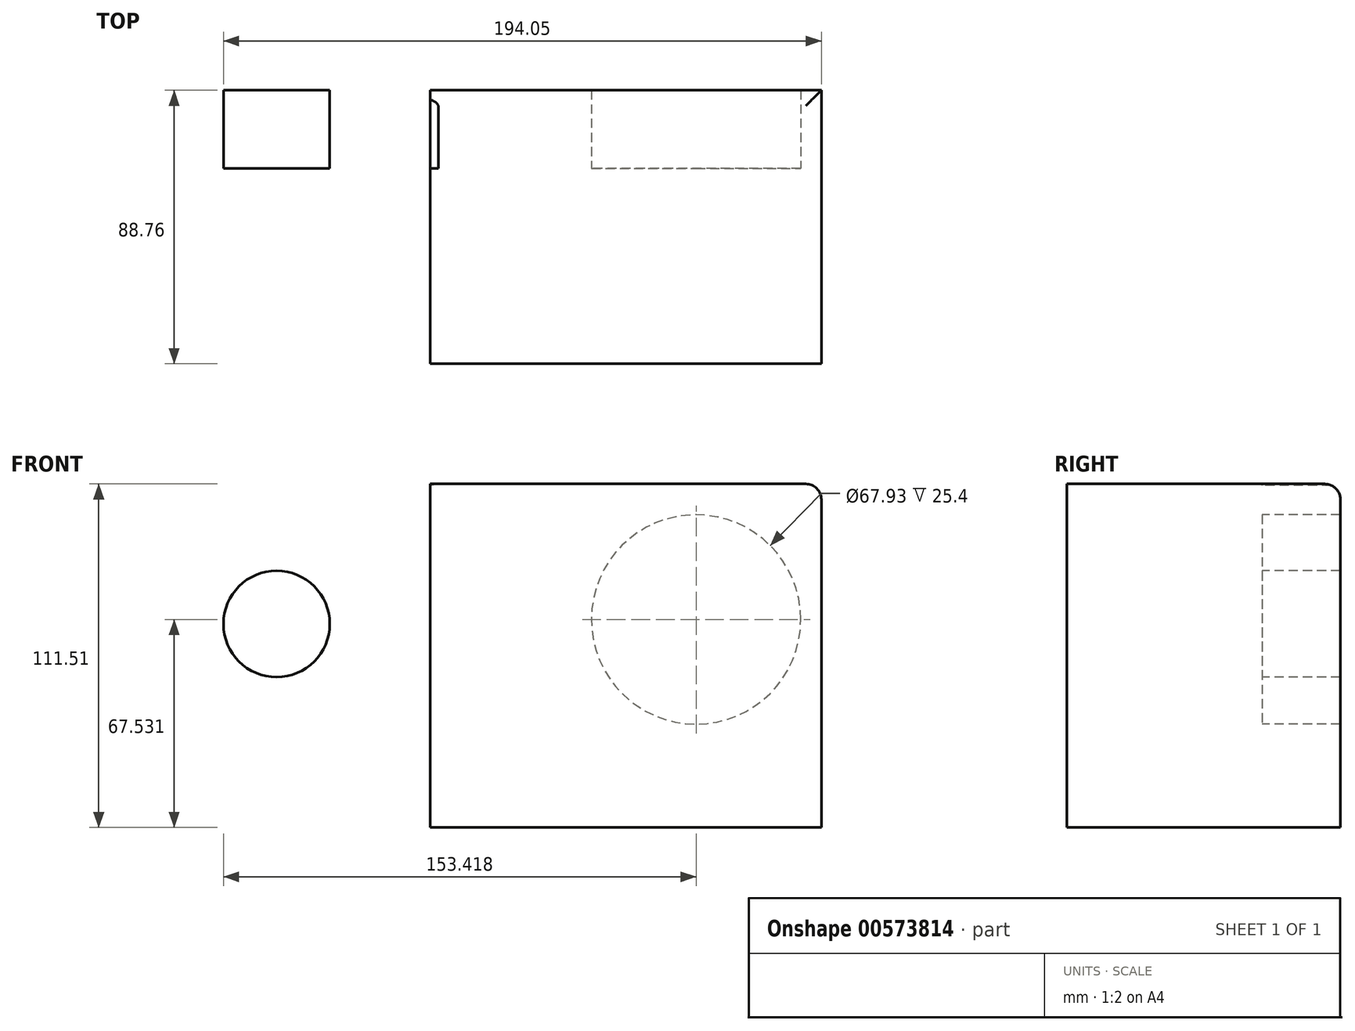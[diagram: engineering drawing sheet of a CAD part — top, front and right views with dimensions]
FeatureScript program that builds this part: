
annotation { "Feature Type Name" : "Feature", "Feature Type Description" : "" }
export const myFeature = defineFeature(function(context is Context, id is Id, definition is map)
    precondition{}
    {
        {
            var Q0;
            Q0=qCreatedBy(makeId("Top.planeOp"),FACE);
            var sketch = newSketch(context, id + "F0", { "sketchPlane" : qUnion([Q0])});
            skLineSegment(sketch, "E0.bottom", {"start": v(-64.53, 22.32) * mm, "end": v(62.39, 22.32) * mm});
            skLineSegment(sketch, "E0.top", {"start": v(-64.53, -41.04) * mm, "end": v(62.39, -41.04) * mm});
            skLineSegment(sketch, "E0.left", {"start": v(-64.53, 22.32) * mm, "end": v(-64.53, -41.04) * mm});
            skLineSegment(sketch, "E0.right", {"start": v(62.39, 22.32) * mm, "end": v(62.39, -41.04) * mm});
            skSolve(sketch);
        }
        {
            var Q0;
            Q0=makeQuery(id+"F0.imprint","IMPRINT",FACE,{"disambiguationData":[TD([[makeQuery(id+"F0.imprint","IMPRINT",EDGE,{"derivedFrom":sQuery(id+"F0.wireOp",EDGE,"E0.bottom")}),-1.0]])]});
            extrude(context, id + "F1", {"entities" : qUnion([Q0]), "depth" : 53.34 * mm, "offsetDistance" : 25.4 * mm});
        }
        {
            var Q0;
            Q0=makeQuery(id+"F1.opExtrude","CAP_FACE",FACE,{"disambiguationData":[OSD([sQuery(id+"F0.wireOp",EDGE,"E0.bottom"),sQuery(id+"F0.wireOp",EDGE,"E0.top"),sQuery(id+"F0.wireOp",EDGE,"E0.left"),sQuery(id+"F0.wireOp",EDGE,"E0.right")])],"isStart":false});
            extrude(context, id + "F2", {"entities" : qUnion([Q0]), "operationType" : NewBodyOperationType.ADD, "depth" : 58.17 * mm, "offsetDistance" : 25.4 * mm});
        }
        {
            var Q0;
            {var subQ0=sQuery(id+"F0.wireOp",EDGE,"E0.bottom");Q0=makeQuery(id+"F2.boolean.opBoolean","MERGE",FACE,{"derivedFrom":[makeQuery(id+"F1.opExtrude","SWEPT_FACE",FACE,{"disambiguationData":[OSD([subQ0])]}),makeQuery(id+"F2.opExtrude","SWEPT_FACE",FACE,{"disambiguationData":[OSD([subQ0])]})]});}
            var sketch = newSketch(context, id + "F3", { "sketchPlane" : qUnion([Q0])});
            skCircle(sketch, "E1", {"center": v(-21.76, 67.53) * mm, "radius": 33.97 * mm});
            skCircle(sketch, "E2", {"center": v(56.17, 72.29) * mm, "radius": 39.64 * mm});
            skCircle(sketch, "E3", {"center": v(114.4, 66.08) * mm, "radius": 17.26 * mm});
            skSolve(sketch);
        }
        {
            var Q0;
            {var subQ0=sQuery(id+"F3.wireOp",EDGE,"E2");var subQ1=sQuery(id+"F0.wireOp",EDGE,"E0.left");var subQ2=sQuery(id+"F0.wireOp",EDGE,"E0.bottom");var subQ3=makeQuery(id+"F2.boolean.opBoolean","MERGE",EDGE,{"derivedFrom":[makeQuery(id+"F1.opExtrude","SWEPT_EDGE",EDGE,{"disambiguationData":[OSD([subQ2,subQ1])]}),makeQuery(id+"F2.opExtrude","SWEPT_EDGE",EDGE,{"disambiguationData":[OSD([subQ2,subQ1])]})]});var subQ4=makeQuery(id+"F3.imprint","INTERSECT",VERTEX,{"disambiguationData":[OD(0.0)],"derivedFrom":[subQ3,subQ0]});Q0=makeQuery(id+"F3.imprint","IMPRINT",FACE,{"disambiguationData":[TD([[makeQuery(id+"F3.imprint","IMPRINT",EDGE,{"disambiguationData":[TD([[subQ4,1.0]])],"derivedFrom":subQ0}),1.0]])]});}
            var Q1;
            Q1=makeQuery(id+"F3.imprint","IMPRINT",FACE,{"disambiguationData":[TD([[makeQuery(id+"F3.imprint","IMPRINT",EDGE,{"derivedFrom":sQuery(id+"F3.wireOp",EDGE,"E3")}),1.0]])]});
            var Q2;
            Q2=makeQuery(id+"F3.imprint","IMPRINT",FACE,{"disambiguationData":[TD([[makeQuery(id+"F3.imprint","IMPRINT",EDGE,{"derivedFrom":sQuery(id+"F3.wireOp",EDGE,"E1")}),-1.0]])]});
            extrude(context, id + "F4", {"entities" : qUnion([Q0, Q1, Q2]), "operationType" : NewBodyOperationType.ADD, "depth" : 25.4 * mm, "offsetDistance" : 25.4 * mm});
        }
        {
            var Q0;
            {var subQ1=sQuery(id+"F0.wireOp",EDGE,"E0.bottom");var subQ2=makeQuery(id+"F2.opExtrude","CAP_EDGE",EDGE,{"disambiguationData":[OSD([subQ1])],"isStart":false});Q0=makeQuery(id+"F4.opExtrude","CAP_EDGE",EDGE,{"disambiguationData":[OSD([subQ1]),TDD([makeQuery(id+"F3.imprint","IMPRINT",EDGE,{"disambiguationData":[TD([[makeQuery(id+"F3.imprint","INTERSECT",VERTEX,{"disambiguationData":[OD(1.0)],"derivedFrom":[subQ2,sQuery(id+"F3.wireOp",EDGE,"E2")]}),-1.0]])],"derivedFrom":subQ2})])],"isStart":false});}
            var Q1;
            {var subQ0=sQuery(id+"F0.wireOp",EDGE,"E0.right");var subQ1=sQuery(id+"F0.wireOp",EDGE,"E0.bottom");Q1=makeQuery(id+"F4.boolean.opBoolean","MERGE",EDGE,{"derivedFrom":[makeQuery(id+"F2.opExtrude","CAP_EDGE",EDGE,{"disambiguationData":[OSD([subQ0])],"isStart":false}),makeQuery(id+"F4.opExtrude","SWEPT_EDGE",EDGE,{"disambiguationData":[OSD([subQ1,subQ0]),TDD([makeQuery(id+"F3.imprint","INTERSECT",VERTEX,{"derivedFrom":[makeQuery(id+"F2.opExtrude","CAP_EDGE",EDGE,{"disambiguationData":[OSD([subQ1])],"isStart":false}),makeQuery(id+"F2.boolean.opBoolean","MERGE",EDGE,{"derivedFrom":[makeQuery(id+"F1.opExtrude","SWEPT_EDGE",EDGE,{"disambiguationData":[OSD([subQ1,subQ0])]}),makeQuery(id+"F2.opExtrude","SWEPT_EDGE",EDGE,{"disambiguationData":[OSD([subQ1,subQ0])]})]})]})])]})]});}
            fillet(context, id + "F5", {"entities" : qUnion([Q0, Q1]), "radius" : 5.08 * mm, "tangentPropagation" : true, "allowEdgeOverflow" : false});
        }
    });
